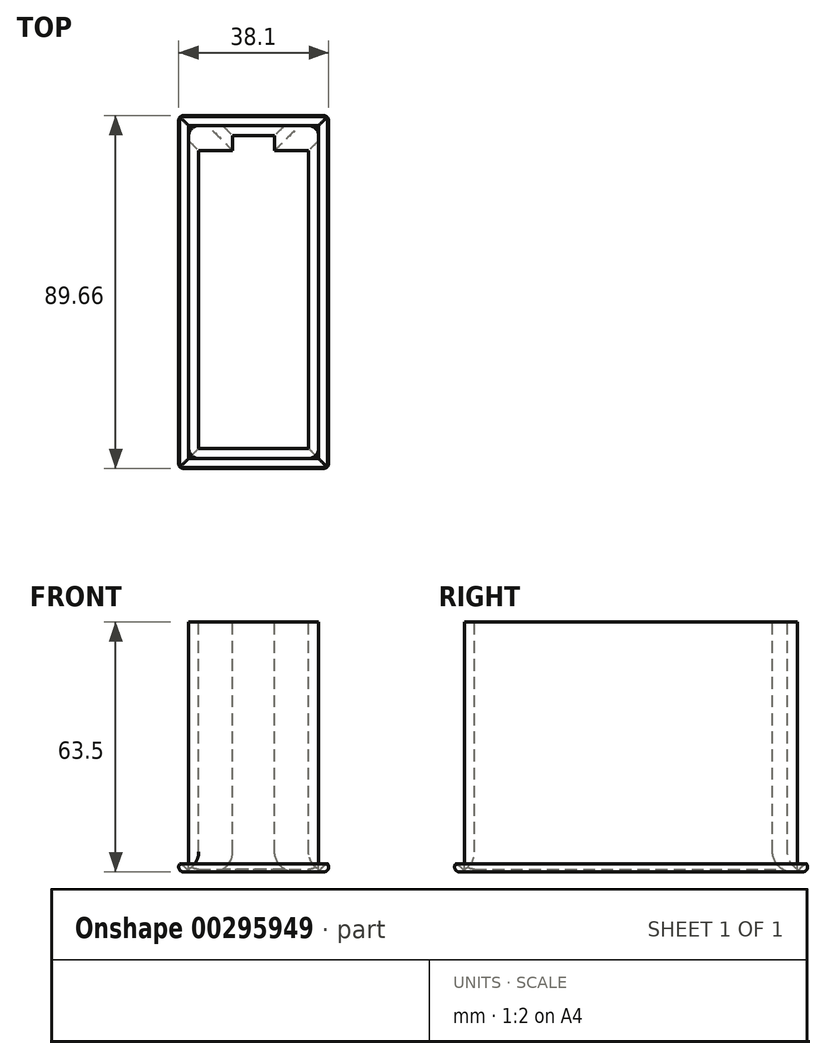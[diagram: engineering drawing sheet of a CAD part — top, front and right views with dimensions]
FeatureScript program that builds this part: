
annotation { "Feature Type Name" : "Feature", "Feature Type Description" : "" }
export const myFeature = defineFeature(function(context is Context, id is Id, definition is map)
    precondition{}
    {
        {
            var Q0;
            Q0=qCreatedBy(makeId("Top.planeOp"),FACE);
            var sketch = newSketch(context, id + "F0", { "sketchPlane" : qUnion([Q0])});
            skLineSegment(sketch, "E0.bottom", {"start": v(16.5, 42.3) * mm, "end": v(-16.51, 42.3) * mm});
            skLineSegment(sketch, "E0.top", {"start": v(16.5, -42.3) * mm, "end": v(-16.5, -42.3) * mm});
            skLineSegment(sketch, "E0.left", {"start": v(16.5, 42.3) * mm, "end": v(16.5, -42.3) * mm});
            skLineSegment(sketch, "E0.right", {"start": v(-16.51, 42.3) * mm, "end": v(-16.51, -42.3) * mm});
            skPoint(sketch, "E0.middle", {"position": v(0, 0) * mm});
            skLineSegment(sketch, "E1.bottom", {"start": v(13.97, 39.75) * mm, "end": v(-13.97, 39.75) * mm});
            skLineSegment(sketch, "E1.top", {"start": v(13.97, -39.75) * mm, "end": v(-13.97, -39.75) * mm});
            skLineSegment(sketch, "E1.left", {"start": v(13.97, 39.75) * mm, "end": v(13.97, -39.75) * mm});
            skLineSegment(sketch, "E1.right", {"start": v(-13.97, 39.75) * mm, "end": v(-13.97, -39.75) * mm});
            skLineSegment(sketch, "E2", {"start": v(-13.97, 35.94) * mm, "end": v(-5.33, 35.94) * mm});
            skLineSegment(sketch, "E3", {"start": v(-5.33, 35.94) * mm, "end": v(-5.33, 39.75) * mm});
            skLineSegment(sketch, "E4", {"start": v(5.33, 39.75) * mm, "end": v(5.33, 35.94) * mm});
            skLineSegment(sketch, "E5", {"start": v(5.33, 35.94) * mm, "end": v(13.97, 35.94) * mm});
            skSolve(sketch);
        }
        {
            var Q0;
            Q0=makeQuery(id+"F0.imprint","IMPRINT",FACE,{"disambiguationData":[TD([[makeQuery(id+"F0.imprint","IMPRINT",EDGE,{"derivedFrom":sQuery(id+"F0.wireOp",EDGE,"E0.bottom")}),1.0]])]});
            var Q1;
            {var subQ4=sQuery(id+"F0.wireOp",EDGE,"E2");Q1=makeQuery(id+"F0.imprint","IMPRINT",FACE,{"disambiguationData":[TD([[makeQuery(id+"F0.imprint","IMPRINT",EDGE,{"derivedFrom":subQ4}),1.0]])]});}
            var Q2;
            {var subQ3=sQuery(id+"F0.wireOp",EDGE,"E4");Q2=makeQuery(id+"F0.imprint","IMPRINT",FACE,{"disambiguationData":[TD([[makeQuery(id+"F0.imprint","IMPRINT",EDGE,{"derivedFrom":subQ3}),1.0]])]});}
            extrude(context, id + "F1", {"entities" : qUnion([Q0, Q1, Q2]), "oppositeDirection" : true, "depth" : 63.5 * mm});
        }
        {
            var Q0;
            Q0=makeQuery(id+"F1.opExtrude","CAP_EDGE",EDGE,{"disambiguationData":[OSD([sQuery(id+"F0.wireOp",EDGE,"E1.bottom")])],"isStart":false});
            var Q1;
            Q1=makeQuery(id+"F1.opExtrude","CAP_EDGE",EDGE,{"disambiguationData":[OSD([sQuery(id+"F0.wireOp",EDGE,"E3")])],"isStart":false});
            var Q2;
            Q2=makeQuery(id+"F1.opExtrude","CAP_EDGE",EDGE,{"disambiguationData":[OSD([sQuery(id+"F0.wireOp",EDGE,"E4")])],"isStart":false});
            var Q3;
            Q3=makeQuery(id+"F1.opExtrude","CAP_EDGE",EDGE,{"disambiguationData":[OSD([sQuery(id+"F0.wireOp",EDGE,"E5")])],"isStart":false});
            var Q4;
            Q4=makeQuery(id+"F1.opExtrude","CAP_EDGE",EDGE,{"disambiguationData":[OSD([sQuery(id+"F0.wireOp",EDGE,"E1.left")])],"isStart":false});
            var Q5;
            Q5=makeQuery(id+"F1.opExtrude","CAP_EDGE",EDGE,{"disambiguationData":[OSD([sQuery(id+"F0.wireOp",EDGE,"E1.right")])],"isStart":false});
            var Q6;
            Q6=makeQuery(id+"F1.opExtrude","CAP_EDGE",EDGE,{"disambiguationData":[OSD([sQuery(id+"F0.wireOp",EDGE,"E1.top")])],"isStart":false});
            var Q7;
            Q7=makeQuery(id+"F1.opExtrude","CAP_EDGE",EDGE,{"disambiguationData":[OSD([sQuery(id+"F0.wireOp",EDGE,"E2")])],"isStart":false});
            fillet(context, id + "F2", {"entities" : qUnion([Q0, Q1, Q2, Q3, Q4, Q5, Q6, Q7]), "radius" : 5.08 * mm, "tangentPropagation" : true, "allowEdgeOverflow" : false});
        }
        {
            var Q0;
            Q0=makeQuery(id+"F2.opFillet","SPLIT",FACE,{"disambiguationData":[OD(1.0)],"derivedFrom":makeQuery(id+"F1.opExtrude","CAP_FACE",FACE,{"disambiguationData":[OSD([sQuery(id+"F0.wireOp",EDGE,"E0.bottom"),sQuery(id+"F0.wireOp",EDGE,"E0.top"),sQuery(id+"F0.wireOp",EDGE,"E0.left"),sQuery(id+"F0.wireOp",EDGE,"E0.right"),sQuery(id+"F0.wireOp",EDGE,"E1.bottom"),sQuery(id+"F0.wireOp",EDGE,"E1.top"),sQuery(id+"F0.wireOp",EDGE,"E1.left"),sQuery(id+"F0.wireOp",EDGE,"E1.right"),sQuery(id+"F0.wireOp",EDGE,"E2"),sQuery(id+"F0.wireOp",EDGE,"E3"),sQuery(id+"F0.wireOp",EDGE,"E4"),sQuery(id+"F0.wireOp",EDGE,"E5")])],"isStart":false})});
            var sketch = newSketch(context, id + "F3", { "sketchPlane" : qUnion([Q0])});
            skLineSegment(sketch, "E6.bottom", {"start": v(19.05, -44.83) * mm, "end": v(-19.05, -44.83) * mm});
            skLineSegment(sketch, "E6.top", {"start": v(19.05, 44.83) * mm, "end": v(-19.05, 44.83) * mm});
            skLineSegment(sketch, "E6.left", {"start": v(19.05, -44.83) * mm, "end": v(19.05, 44.83) * mm});
            skLineSegment(sketch, "E6.right", {"start": v(-19.05, -44.83) * mm, "end": v(-19.05, 44.83) * mm});
            skPoint(sketch, "E6.middle", {"position": v(0, 0) * mm});
            skLineSegment(sketch, "E7.bottom", {"start": v(16.5, 42.3) * mm, "end": v(-16.5, 42.3) * mm});
            skLineSegment(sketch, "E7.top", {"start": v(16.5, -42.3) * mm, "end": v(-16.5, -42.3) * mm});
            skLineSegment(sketch, "E7.left", {"start": v(16.5, 42.3) * mm, "end": v(16.5, -42.3) * mm});
            skLineSegment(sketch, "E7.right", {"start": v(-16.5, 42.3) * mm, "end": v(-16.5, -42.3) * mm});
            skSolve(sketch);
        }
        {
            var Q0;
            Q0 = qSketchRegion(id + "F3", true);
            extrude(context, id + "F4", {"entities" : qUnion([Q0]), "oppositeDirection" : true, "depth" : 2.54 * mm});
        }
        {
            var Q0;
            Q0=makeQuery(id+"F4.opExtrude","CAP_EDGE",EDGE,{"disambiguationData":[OSD([sQuery(id+"F3.wireOp",EDGE,"E6.top")])],"isStart":true});
            var Q1;
            Q1=makeQuery(id+"F4.opExtrude","CAP_EDGE",EDGE,{"disambiguationData":[OSD([sQuery(id+"F3.wireOp",EDGE,"E6.left")])],"isStart":true});
            var Q2;
            Q2=makeQuery(id+"F4.opExtrude","CAP_EDGE",EDGE,{"disambiguationData":[OSD([sQuery(id+"F3.wireOp",EDGE,"E6.left")])],"isStart":false});
            var Q3;
            Q3=makeQuery(id+"F4.opExtrude","CAP_EDGE",EDGE,{"disambiguationData":[OSD([sQuery(id+"F3.wireOp",EDGE,"E6.bottom")])],"isStart":true});
            var Q4;
            Q4=makeQuery(id+"F4.opExtrude","CAP_EDGE",EDGE,{"disambiguationData":[OSD([sQuery(id+"F3.wireOp",EDGE,"E6.right")])],"isStart":true});
            var Q5;
            Q5=makeQuery(id+"F4.opExtrude","CAP_EDGE",EDGE,{"disambiguationData":[OSD([sQuery(id+"F3.wireOp",EDGE,"E6.right")])],"isStart":false});
            var Q6;
            Q6=makeQuery(id+"F4.opExtrude","CAP_EDGE",EDGE,{"disambiguationData":[OSD([sQuery(id+"F3.wireOp",EDGE,"E6.top")])],"isStart":false});
            var Q7;
            Q7=makeQuery(id+"F4.opExtrude","SWEPT_EDGE",EDGE,{"disambiguationData":[OSD([sQuery(id+"F3.wireOp",EDGE,"E6.top"),sQuery(id+"F3.wireOp",EDGE,"E6.right")])]});
            var Q8;
            Q8=makeQuery(id+"F4.opExtrude","SWEPT_EDGE",EDGE,{"disambiguationData":[OSD([sQuery(id+"F3.wireOp",EDGE,"E6.top"),sQuery(id+"F3.wireOp",EDGE,"E6.left")])]});
            var Q9;
            Q9=makeQuery(id+"F4.opExtrude","SWEPT_EDGE",EDGE,{"disambiguationData":[OSD([sQuery(id+"F3.wireOp",EDGE,"E6.bottom"),sQuery(id+"F3.wireOp",EDGE,"E6.right")])]});
            var Q10;
            Q10=makeQuery(id+"F4.opExtrude","SWEPT_EDGE",EDGE,{"disambiguationData":[OSD([sQuery(id+"F3.wireOp",EDGE,"E6.bottom"),sQuery(id+"F3.wireOp",EDGE,"E6.left")])]});
            var Q11;
            Q11=makeQuery(id+"F4.opExtrude","CAP_EDGE",EDGE,{"disambiguationData":[OSD([sQuery(id+"F3.wireOp",EDGE,"E6.bottom")])],"isStart":false});
            fillet(context, id + "F5", {"entities" : qUnion([Q0, Q1, Q2, Q3, Q4, Q5, Q6, Q7, Q8, Q9, Q10, Q11]), "radius" : 1.27 * mm, "tangentPropagation" : true, "allowEdgeOverflow" : false});
        }
        {
            var Q0;
            Q0=makeQuery(id+"F4.opExtrude","CAP_EDGE",EDGE,{"disambiguationData":[OSD([sQuery(id+"F3.wireOp",EDGE,"E7.top")])],"isStart":false});
            var Q1;
            Q1=makeQuery(id+"F4.opExtrude","CAP_EDGE",EDGE,{"disambiguationData":[OSD([sQuery(id+"F3.wireOp",EDGE,"E7.left")])],"isStart":false});
            var Q2;
            Q2=makeQuery(id+"F4.opExtrude","CAP_EDGE",EDGE,{"disambiguationData":[OSD([sQuery(id+"F3.wireOp",EDGE,"E7.bottom")])],"isStart":false});
            var Q3;
            Q3=makeQuery(id+"F4.opExtrude","CAP_EDGE",EDGE,{"disambiguationData":[OSD([sQuery(id+"F3.wireOp",EDGE,"E7.right")])],"isStart":false});
            fillet(context, id + "F6", {"entities" : qUnion([Q0, Q1, Q2, Q3]), "radius" : 5.08 * mm, "tangentPropagation" : true, "allowEdgeOverflow" : false});
        }
        {
            var Q0;
            Q0=makeQuery(id+"F1.opExtrude","SWEPT_EDGE",EDGE,{"disambiguationData":[OSD([sQuery(id+"F0.wireOp",EDGE,"E0.top"),sQuery(id+"F0.wireOp",EDGE,"E0.left")])]});
            var Q1;
            Q1=makeQuery(id+"F1.opExtrude","SWEPT_EDGE",EDGE,{"disambiguationData":[OSD([sQuery(id+"F0.wireOp",EDGE,"E0.top"),sQuery(id+"F0.wireOp",EDGE,"E0.right")])]});
            var Q2;
            Q2=makeQuery(id+"F1.opExtrude","SWEPT_EDGE",EDGE,{"disambiguationData":[OSD([sQuery(id+"F0.wireOp",EDGE,"E0.bottom"),sQuery(id+"F0.wireOp",EDGE,"E0.left")])]});
            var Q3;
            Q3=makeQuery(id+"F1.opExtrude","SWEPT_EDGE",EDGE,{"disambiguationData":[OSD([sQuery(id+"F0.wireOp",EDGE,"E0.bottom"),sQuery(id+"F0.wireOp",EDGE,"E0.right")])]});
            fillet(context, id + "F7", {"entities" : qUnion([Q0, Q1, Q2, Q3]), "radius" : 2.54 * mm, "allowEdgeOverflow" : false});
        }
    });
